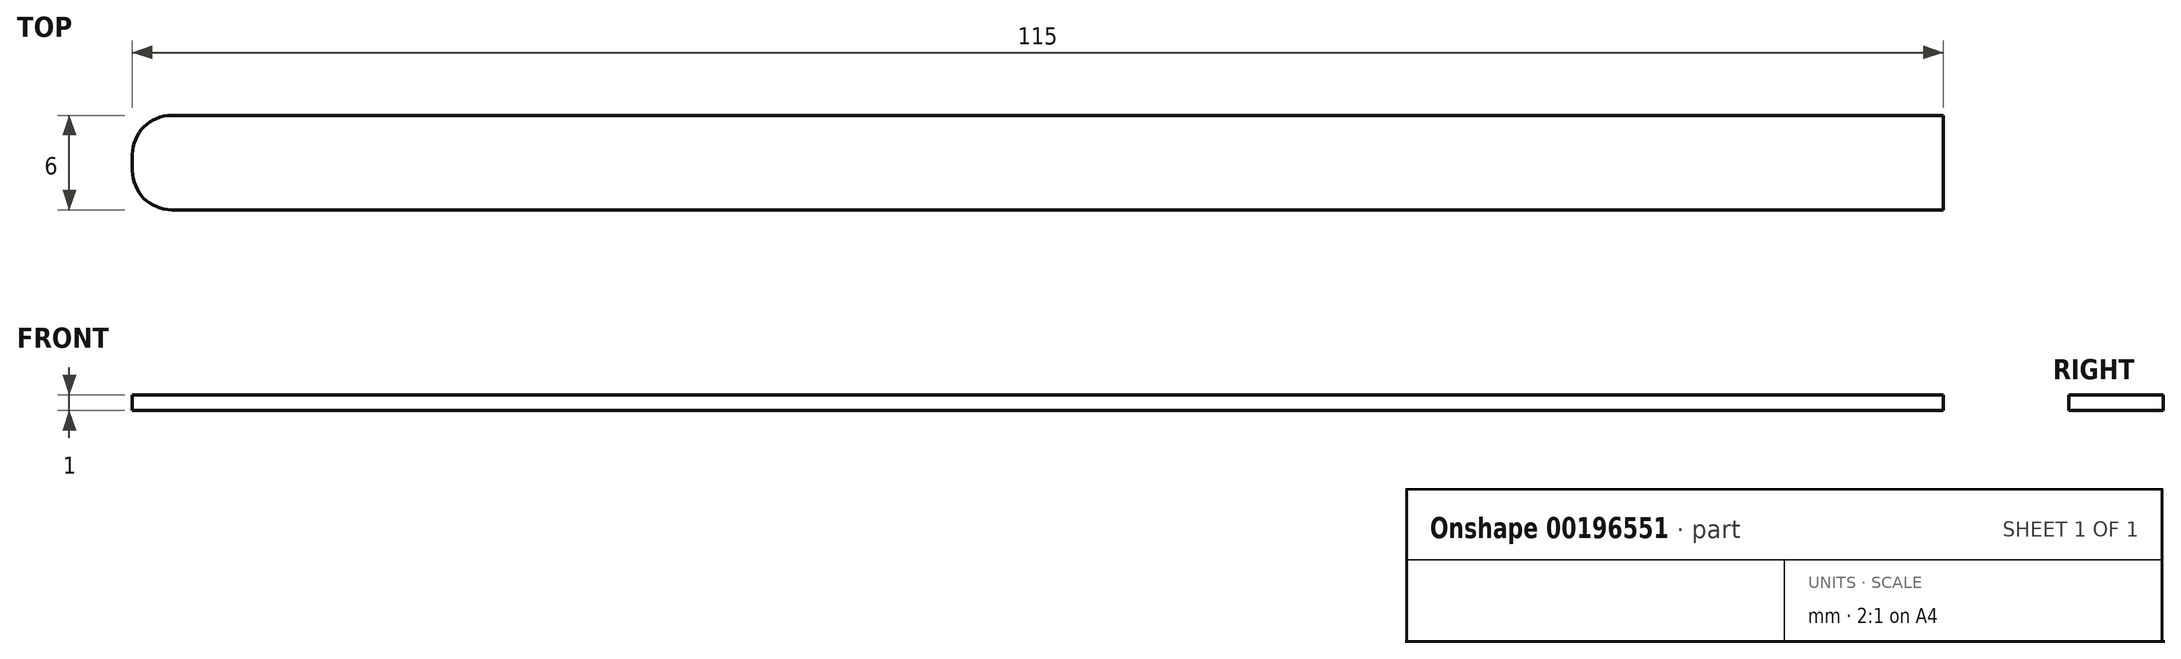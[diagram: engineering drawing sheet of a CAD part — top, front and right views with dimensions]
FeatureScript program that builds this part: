
annotation { "Feature Type Name" : "Feature", "Feature Type Description" : "" }
export const myFeature = defineFeature(function(context is Context, id is Id, definition is map)
    precondition{}
    {
        {
            var Q0;
            Q0=qCreatedBy(makeId("Top.planeOp"),FACE);
            var sketch = newSketch(context, id + "F0", { "sketchPlane" : qUnion([Q0])});
            skLineSegment(sketch, "E0.bottom", {"start": v(-56.25, 0) * mm, "end": v(56.25, 0) * mm});
            skLineSegment(sketch, "E0.top", {"start": v(-56.25, -6) * mm, "end": v(56.25, -6) * mm});
            skLineSegment(sketch, "E0.left", {"start": v(-58.75, -2.5) * mm, "end": v(-58.75, -3.5) * mm});
            skLineSegment(sketch, "E0.right", {"start": v(56.25, 0) * mm, "end": v(56.25, -6) * mm});
            skPoint(sketch, "E1.visualSharp", {"position": v(-58.75, 0) * mm});
            skArc(sketch, "E1.filletArc", {"start": v(-56.25, 0) * mm, "mid": v(-58.02, -0.73) * mm, "end": v(-58.75, -2.5) * mm});
            skPoint(sketch, "E2.visualSharp", {"position": v(-58.75, -6) * mm});
            skArc(sketch, "E2.filletArc", {"start": v(-58.75, -3.5) * mm, "mid": v(-58.02, -5.27) * mm, "end": v(-56.25, -6) * mm});
            skSolve(sketch);
        }
        {
            var Q0;
            Q0=makeQuery(id+"F0.imprint","IMPRINT",FACE,{"disambiguationData":[TD([[makeQuery(id+"F0.imprint","IMPRINT",EDGE,{"derivedFrom":sQuery(id+"F0.wireOp",EDGE,"E0.bottom")}),-1.0]])]});
            extrude(context, id + "F1", {"entities" : qUnion([Q0]), "depth" : 1 * mm});
        }
    });
